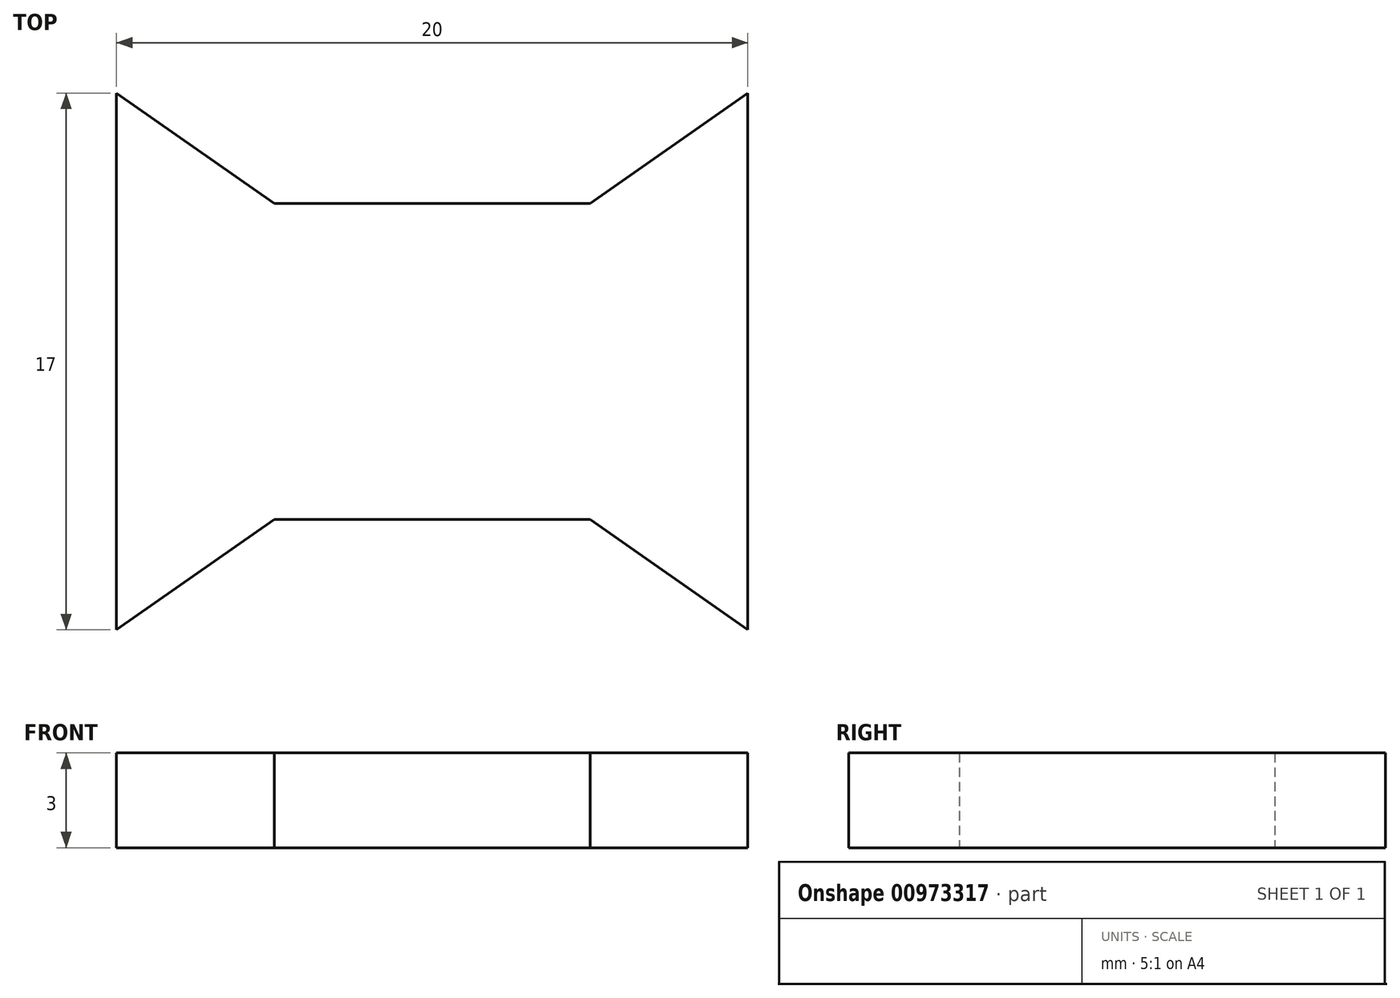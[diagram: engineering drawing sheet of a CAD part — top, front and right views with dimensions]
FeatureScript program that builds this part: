
annotation { "Feature Type Name" : "Feature", "Feature Type Description" : "" }
export const myFeature = defineFeature(function(context is Context, id is Id, definition is map)
    precondition{}
    {
        {
            var Q0;
            Q0=qCreatedBy(makeId("Top.planeOp"),FACE);
            var sketch = newSketch(context, id + "F0", { "sketchPlane" : qUnion([Q0])});
            skLineSegment(sketch, "E0.bottom", {"start": v(-5, 5) * mm, "end": v(5, 5) * mm});
            skLineSegment(sketch, "E0.top", {"start": v(-5, -5) * mm, "end": v(5, -5) * mm});
            skLineSegment(sketch, "E0.left", {"start": v(-5, 5) * mm, "end": v(-5, -5) * mm});
            skLineSegment(sketch, "E0.right", {"start": v(5, 5) * mm, "end": v(5, -5) * mm});
            skLineSegment(sketch, "E1.bottom", {"start": v(-5, 5) * mm, "end": v(-10, 5) * mm});
            skLineSegment(sketch, "E1.top", {"start": v(-5, -5) * mm, "end": v(-10, -5) * mm});
            skLineSegment(sketch, "E1.right", {"start": v(-10, 5) * mm, "end": v(-10, -5) * mm});
            skLineSegment(sketch, "E2", {"start": v(-10, -5) * mm, "end": v(-10, -8.5) * mm});
            skLineSegment(sketch, "E3", {"start": v(-5, -5) * mm, "end": v(-10, -8.5) * mm});
            skLineSegment(sketch, "E4.MirrorCS", {"start": v(-5, 5) * mm, "end": v(-10, 8.5) * mm});
            skLineSegment(sketch, "E5.MirrorCS", {"start": v(-10, 5) * mm, "end": v(-10, 8.5) * mm});
            skLineSegment(sketch, "E6.MirrorCS", {"start": v(10, 5) * mm, "end": v(10, -5) * mm});
            skLineSegment(sketch, "E7.MirrorCS", {"start": v(5, -5) * mm, "end": v(10, -8.5) * mm});
            skLineSegment(sketch, "E8.MirrorCS", {"start": v(10, -5) * mm, "end": v(10, -8.5) * mm});
            skLineSegment(sketch, "E9.MirrorCS", {"start": v(5, 5) * mm, "end": v(10, 8.5) * mm});
            skLineSegment(sketch, "E10.MirrorCS", {"start": v(10, 5) * mm, "end": v(10, 8.5) * mm});
            skSolve(sketch);
        }
        {
            var Q0;
            Q0=makeQuery(id+"F0.imprint","IMPRINT",FACE,{"disambiguationData":[TD([[makeQuery(id+"F0.imprint","IMPRINT",EDGE,{"derivedFrom":sQuery(id+"F0.wireOp",EDGE,"E0.right")}),1.0]])]});
            var Q1;
            Q1=makeQuery(id+"F0.imprint","IMPRINT",FACE,{"disambiguationData":[TD([[makeQuery(id+"F0.imprint","IMPRINT",EDGE,{"derivedFrom":sQuery(id+"F0.wireOp",EDGE,"E0.bottom")}),-1.0]])]});
            var Q2;
            Q2=makeQuery(id+"F0.imprint","IMPRINT",FACE,{"disambiguationData":[TD([[makeQuery(id+"F0.imprint","IMPRINT",EDGE,{"derivedFrom":sQuery(id+"F0.wireOp",EDGE,"E1.bottom")}),1.0]])]});
            var Q3;
            Q3=makeQuery(id+"F0.imprint","IMPRINT",FACE,{"disambiguationData":[TD([[makeQuery(id+"F0.imprint","IMPRINT",EDGE,{"derivedFrom":sQuery(id+"F0.wireOp",EDGE,"E1.top")}),1.0]])]});
            var Q4;
            Q4=makeQuery(id+"F0.imprint","IMPRINT",FACE,{"disambiguationData":[TD([[makeQuery(id+"F0.imprint","IMPRINT",EDGE,{"derivedFrom":sQuery(id+"F0.wireOp",EDGE,"E1.bottom")}),-1.0]])]});
            extrude(context, id + "F1", {"entities" : qUnion([Q0, Q1, Q2, Q3, Q4]), "depth" : 3 * mm, "offsetDistance" : 25 * mm});
        }
    });
